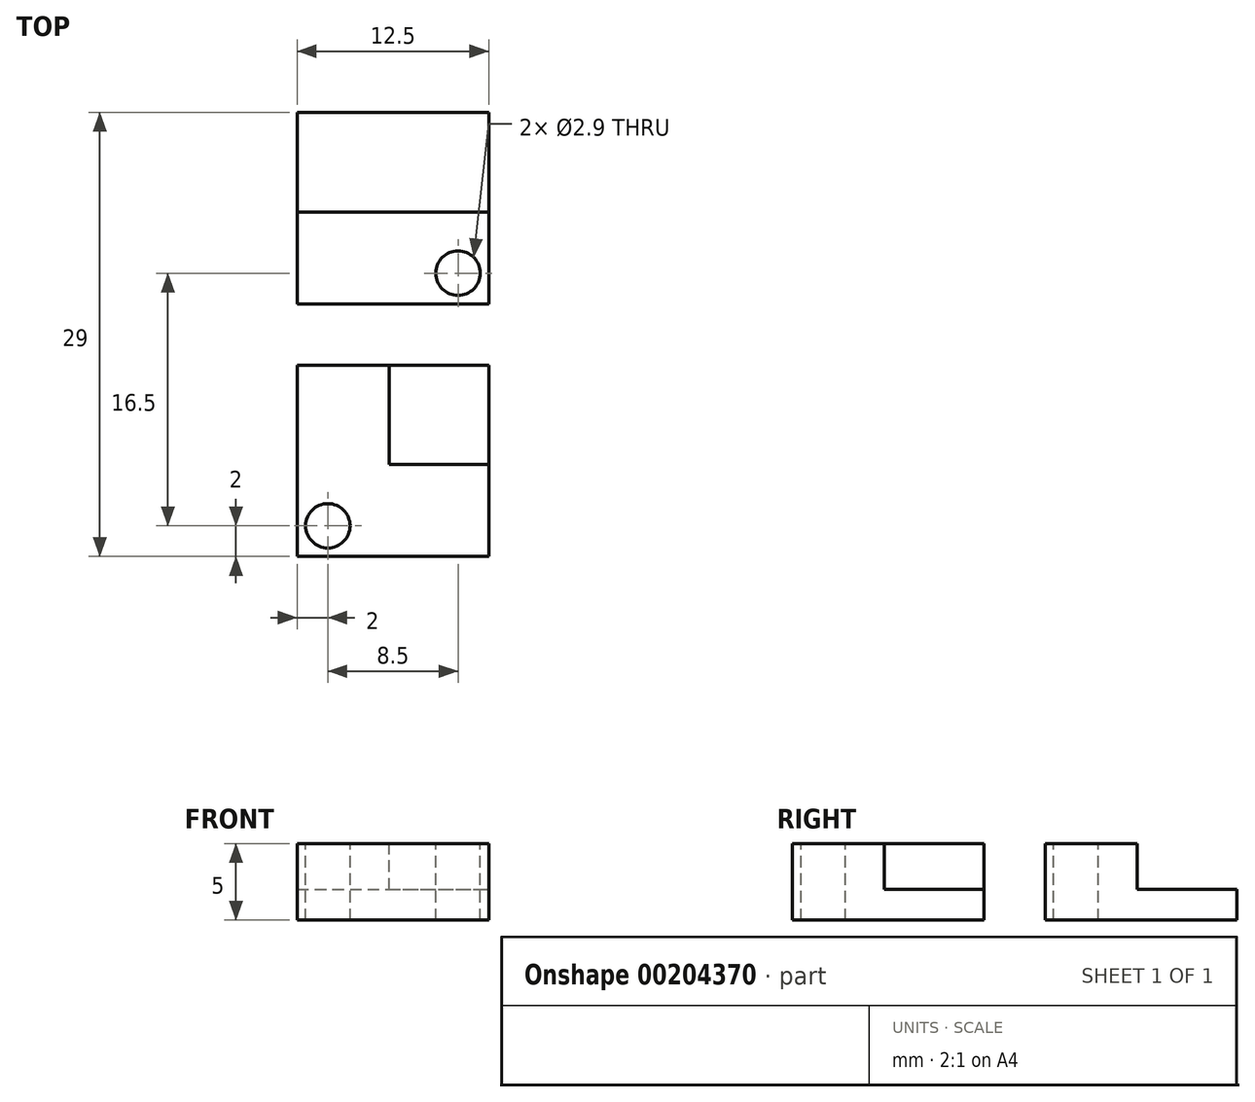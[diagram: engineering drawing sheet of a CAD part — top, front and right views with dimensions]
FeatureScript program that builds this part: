
annotation { "Feature Type Name" : "Feature", "Feature Type Description" : "" }
export const myFeature = defineFeature(function(context is Context, id is Id, definition is map)
    precondition{}
    {
        {
            var Q0;
            Q0=qCreatedBy(makeId("Top.planeOp"),FACE);
            var sketch = newSketch(context, id + "F0", { "sketchPlane" : qUnion([Q0])});
            skLineSegment(sketch, "E0.bottom", {"start": v(0, 0) * mm, "end": v(12.5, 0) * mm});
            skLineSegment(sketch, "E0.top", {"start": v(0, 12.5) * mm, "end": v(12.5, 12.5) * mm});
            skLineSegment(sketch, "E0.left", {"start": v(0, 0) * mm, "end": v(0, 12.5) * mm});
            skLineSegment(sketch, "E0.right", {"start": v(12.5, 0) * mm, "end": v(12.5, 12.5) * mm});
            skSolve(sketch);
        }
        {
            var Q0;
            Q0=makeQuery(id+"F0.imprint","IMPRINT",FACE,{"disambiguationData":[TD([[makeQuery(id+"F0.imprint","IMPRINT",EDGE,{"derivedFrom":sQuery(id+"F0.wireOp",EDGE,"E0.bottom")}),1.0]])]});
            extrude(context, id + "F1", {"entities" : qUnion([Q0]), "depth" : 5 * mm});
        }
        {
            var Q0;
            Q0=makeQuery(id+"F1.opExtrude","CAP_FACE",FACE,{"disambiguationData":[OSD([sQuery(id+"F0.wireOp",EDGE,"E0.bottom"),sQuery(id+"F0.wireOp",EDGE,"E0.top"),sQuery(id+"F0.wireOp",EDGE,"E0.left"),sQuery(id+"F0.wireOp",EDGE,"E0.right")])],"isStart":false});
            var sketch = newSketch(context, id + "F2", { "sketchPlane" : qUnion([Q0])});
            skLineSegment(sketch, "E1.bottom", {"start": v(12.5, 12.5) * mm, "end": v(6, 12.5) * mm});
            skLineSegment(sketch, "E1.top", {"start": v(12.5, 6) * mm, "end": v(6, 6) * mm});
            skLineSegment(sketch, "E1.left", {"start": v(12.5, 12.5) * mm, "end": v(12.5, 6) * mm});
            skLineSegment(sketch, "E1.right", {"start": v(6, 12.5) * mm, "end": v(6, 6) * mm});
            skSolve(sketch);
        }
        {
            var Q0;
            Q0=makeQuery(id+"F2.imprint","IMPRINT",FACE,{"disambiguationData":[TD([[makeQuery(id+"F2.imprint","IMPRINT",EDGE,{"derivedFrom":sQuery(id+"F2.wireOp",EDGE,"E1.bottom")}),-1.0]])]});
            extrude(context, id + "F3", {"entities" : qUnion([Q0]), "operationType" : NewBodyOperationType.REMOVE, "oppositeDirection" : true, "depth" : 3 * mm});
        }
        {
            var Q0;
            Q0=makeQuery(id+"F1.opExtrude","CAP_FACE",FACE,{"disambiguationData":[OSD([sQuery(id+"F0.wireOp",EDGE,"E0.bottom"),sQuery(id+"F0.wireOp",EDGE,"E0.top"),sQuery(id+"F0.wireOp",EDGE,"E0.left"),sQuery(id+"F0.wireOp",EDGE,"E0.right")])],"isStart":false});
            var sketch = newSketch(context, id + "F4", { "sketchPlane" : qUnion([Q0])});
            skCircle(sketch, "E2", {"center": v(2, 2) * mm, "radius": 1.45 * mm});
            skSolve(sketch);
        }
        {
            var Q0;
            Q0=makeQuery(id+"F4.imprint","IMPRINT",FACE,{"disambiguationData":[TD([[makeQuery(id+"F4.imprint","IMPRINT",EDGE,{"derivedFrom":sQuery(id+"F4.wireOp",EDGE,"E2")}),1.0]])]});
            extrude(context, id + "F5", {"entities" : qUnion([Q0]), "operationType" : NewBodyOperationType.REMOVE, "endBound" : BoundingType.THROUGH_ALL, "oppositeDirection" : true, "depth" : 25 * mm});
        }
        {
            var Q0;
            Q0=makeQuery(id+"F1.opExtrude","SWEPT_BODY",BODY,{"disambiguationData":[OSD([sQuery(id+"F0.wireOp",EDGE,"E0.bottom"),sQuery(id+"F0.wireOp",EDGE,"E0.top"),sQuery(id+"F0.wireOp",EDGE,"E0.left"),sQuery(id+"F0.wireOp",EDGE,"E0.right")])]});
            transform(context, id + "F6", {"entities" : qUnion([Q0]), "transformType" : TransformType.TRANSLATION_3D, "dx" : 0 * mm, "dy" : 16.5 * mm, "dz" : 0 * mm, "makeCopy" : true});
        }
        {
            var Q0;
            Q0=makeQuery(id+"F6.opPattern","COPY",FACE,{"derivedFrom":makeQuery(id+"F3.boolean.opBoolean","COPY",FACE,{"derivedFrom":makeQuery(id+"F3.opExtrude","SWEPT_FACE",FACE,{"disambiguationData":[OSD([sQuery(id+"F2.wireOp",EDGE,"E1.right")])]})}),"instanceName":"1"});
            extrude(context, id + "F7", {"entities" : qUnion([Q0]), "operationType" : NewBodyOperationType.REMOVE, "endBound" : BoundingType.THROUGH_ALL, "oppositeDirection" : true, "depth" : 25 * mm});
        }
        {
            var Q0;
            Q0=makeQuery(id+"F6.opPattern","COPY",FACE,{"derivedFrom":makeQuery(id+"F1.opExtrude","CAP_FACE",FACE,{"disambiguationData":[OSD([sQuery(id+"F0.wireOp",EDGE,"E0.bottom"),sQuery(id+"F0.wireOp",EDGE,"E0.top"),sQuery(id+"F0.wireOp",EDGE,"E0.left"),sQuery(id+"F0.wireOp",EDGE,"E0.right")])],"isStart":false}),"instanceName":"1"});
            var sketch = newSketch(context, id + "F8", { "sketchPlane" : qUnion([Q0])});
            skCircle(sketch, "E3.0", {"center": v(2, 18.5) * mm, "radius": 1.45 * mm});
            skCircle(sketch, "E4", {"center": v(10.5, 18.5) * mm, "radius": 1.45 * mm});
            skSolve(sketch);
        }
        {
            var Q0;
            Q0=makeQuery(id+"F8.imprint","IMPRINT",FACE,{"disambiguationData":[TD([[makeQuery(id+"F8.imprint","IMPRINT",EDGE,{"derivedFrom":sQuery(id+"F8.wireOp",EDGE,"E3.0")}),1.0]])]});
            extrude(context, id + "F9", {"entities" : qUnion([Q0]), "operationType" : NewBodyOperationType.ADD, "oppositeDirection" : true, "depth" : 5 * mm});
        }
        {
            var Q0;
            Q0=makeQuery(id+"F8.imprint","IMPRINT",FACE,{"disambiguationData":[TD([[makeQuery(id+"F8.imprint","IMPRINT",EDGE,{"derivedFrom":sQuery(id+"F8.wireOp",EDGE,"E4")}),1.0]])]});
            extrude(context, id + "F10", {"entities" : qUnion([Q0]), "operationType" : NewBodyOperationType.REMOVE, "endBound" : BoundingType.THROUGH_ALL, "oppositeDirection" : true, "depth" : 25 * mm});
        }
    });
